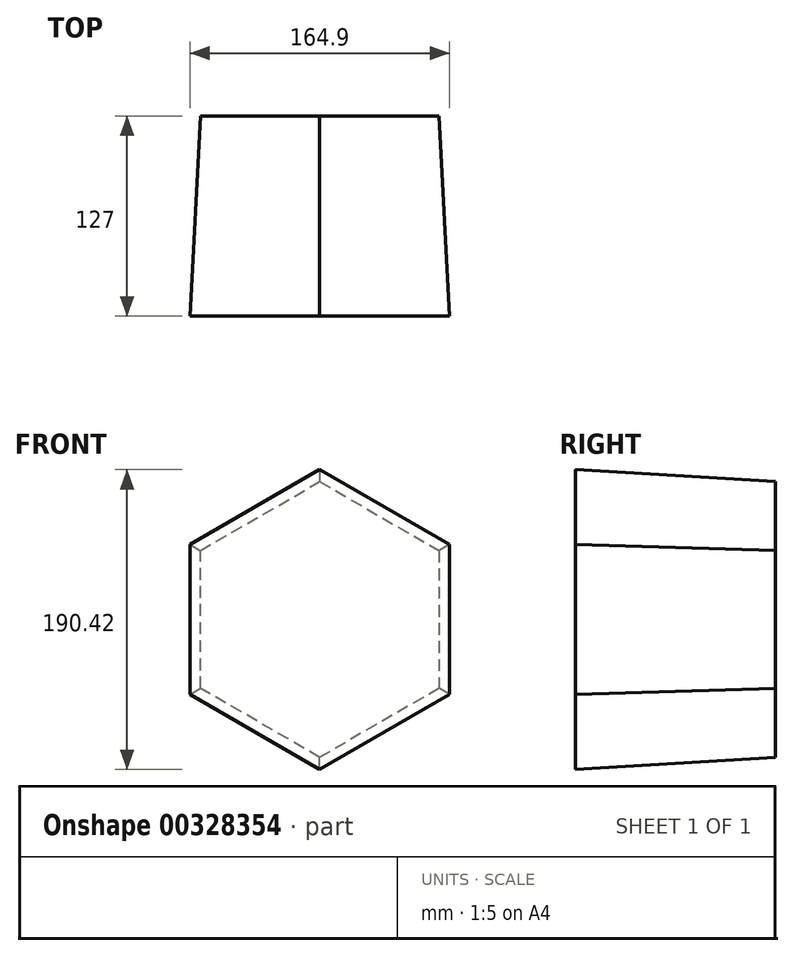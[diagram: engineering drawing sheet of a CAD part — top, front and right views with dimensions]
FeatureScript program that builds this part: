
annotation { "Feature Type Name" : "Feature", "Feature Type Description" : "" }
export const myFeature = defineFeature(function(context is Context, id is Id, definition is map)
    precondition{}
    {
        {
            var Q0;
            Q0=qCreatedBy(makeId("Front.planeOp"),FACE);
            var sketch = newSketch(context, id + "F0", { "sketchPlane" : qUnion([Q0])});
            skCircle(sketch, "E0.cCircle", {"center": v(0, 0) * mm, "radius": 75.8 * mm, "construction": true});
            skLineSegment(sketch, "E0.0", {"start": v(75.8, 43.76) * mm, "end": v(75.8, -43.76) * mm});
            skLineSegment(sketch, "E0.1", {"start": v(75.8, -43.76) * mm, "end": v(0, -87.53) * mm});
            skLineSegment(sketch, "E0.2", {"start": v(0, -87.53) * mm, "end": v(-75.8, -43.76) * mm});
            skLineSegment(sketch, "E0.3", {"start": v(-75.8, -43.76) * mm, "end": v(-75.8, 43.76) * mm});
            skLineSegment(sketch, "E0.4", {"start": v(-75.8, 43.76) * mm, "end": v(0, 87.53) * mm});
            skLineSegment(sketch, "E0.5", {"start": v(0, 87.53) * mm, "end": v(75.8, 43.76) * mm});
            skPoint(sketch, "E0.0.midPoint", {"position": v(75.8, 0) * mm});
            skSolve(sketch);
        }
        {
            var Q0;
            Q0=makeQuery(id+"F0.imprint","IMPRINT",FACE,{"disambiguationData":[TD([[makeQuery(id+"F0.imprint","IMPRINT",EDGE,{"derivedFrom":sQuery(id+"F0.wireOp",EDGE,"E0.0")}),-1.0]])]});
            extrude(context, id + "F1", {"entities" : qUnion([Q0]), "depth" : 127 * mm, "hasDraft" : true, "draftAngle" : 3 * degree});
        }
    });
